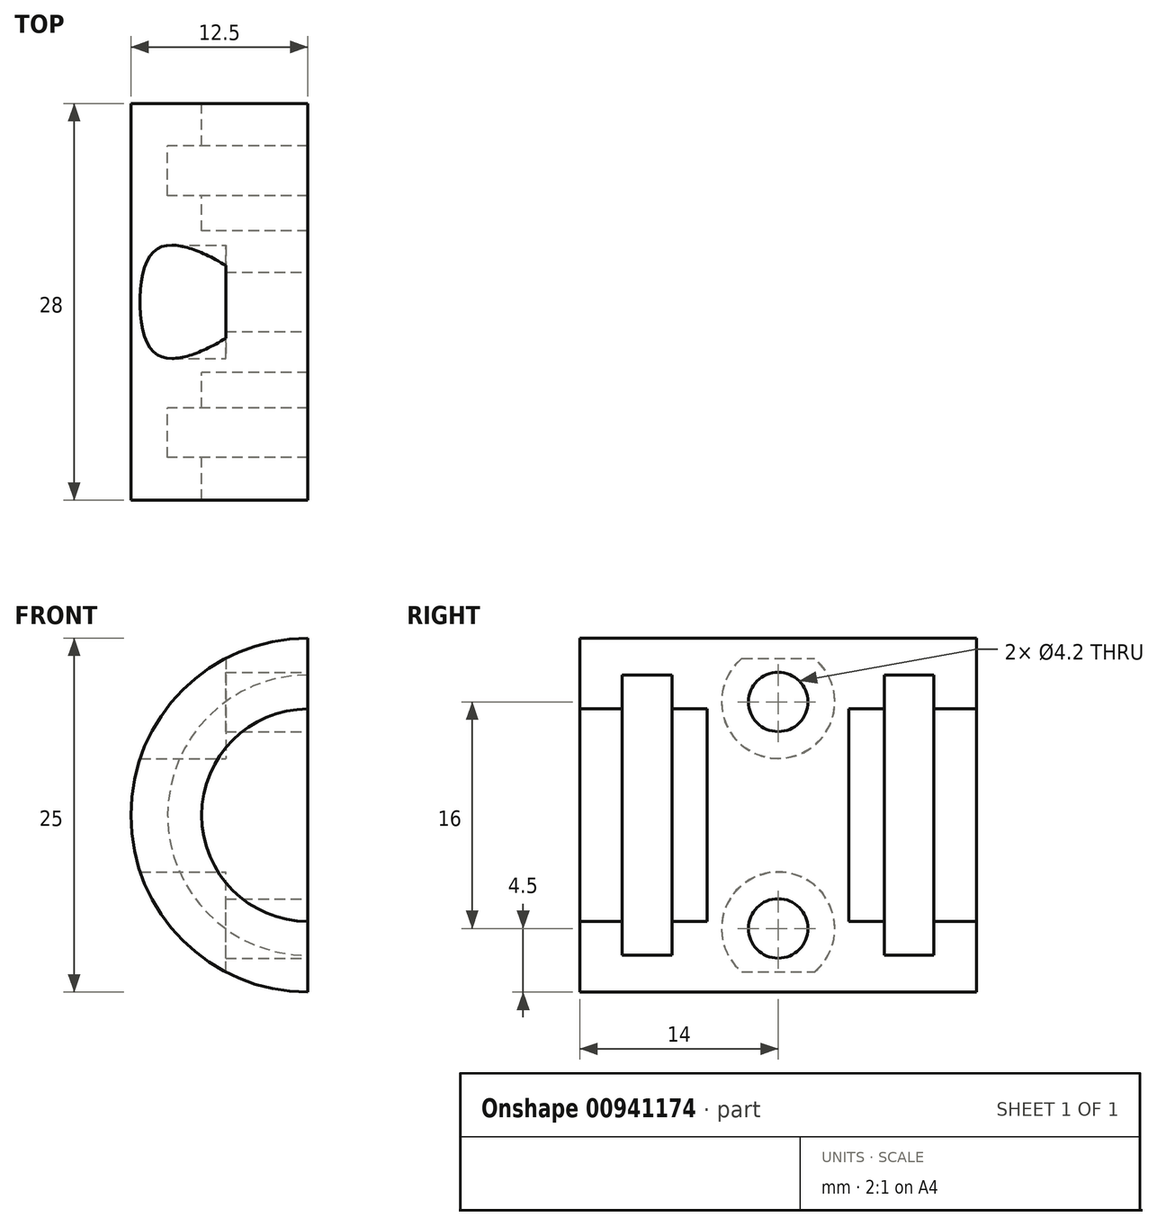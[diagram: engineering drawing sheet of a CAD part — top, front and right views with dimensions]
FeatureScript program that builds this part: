
annotation { "Feature Type Name" : "Feature", "Feature Type Description" : "" }
export const myFeature = defineFeature(function(context is Context, id is Id, definition is map)
    precondition{}
    {
        {
            var Q0;
            Q0=qCreatedBy(makeId("Front.planeOp"),FACE);
            var sketch = newSketch(context, id + "F0", { "sketchPlane" : qUnion([Q0])});
            skCircle(sketch, "E0", {"center": v(0, 0) * mm, "radius": 12.5 * mm});
            skCircle(sketch, "E1", {"center": v(0, 0) * mm, "radius": 7.5 * mm});
            skSolve(sketch);
        }
        {
            var Q0;
            Q0=makeQuery(id+"F0.imprint","IMPRINT",FACE,{"disambiguationData":[TD([[makeQuery(id+"F0.imprint","IMPRINT",EDGE,{"derivedFrom":sQuery(id+"F0.wireOp",EDGE,"E0")}),1.0]])]});
            extrude(context, id + "F1", {"entities" : qUnion([Q0]), "depth" : 28 * mm, "offsetDistance" : 25 * mm});
        }
        {
            var Q0;
            Q0=qCreatedBy(makeId("Right.planeOp"),FACE);
            var sketch = newSketch(context, id + "F2", { "sketchPlane" : qUnion([Q0])});
            skLineSegment(sketch, "E2.bottom", {"start": v(-21.5, 9.9) * mm, "end": v(-25, 9.9) * mm});
            skLineSegment(sketch, "E2.top", {"start": v(-21.5, -9.9) * mm, "end": v(-25, -9.9) * mm});
            skLineSegment(sketch, "E2.left", {"start": v(-21.5, 9.9) * mm, "end": v(-21.5, -9.9) * mm});
            skLineSegment(sketch, "E2.right", {"start": v(-25, 9.9) * mm, "end": v(-25, -9.9) * mm});
            skPoint(sketch, "E2.middle", {"position": v(-23.25, 0) * mm});
            skLineSegment(sketch, "E3.bottom", {"start": v(-3, 9.9) * mm, "end": v(-6.5, 9.9) * mm});
            skLineSegment(sketch, "E3.top", {"start": v(-3, -9.9) * mm, "end": v(-6.5, -9.9) * mm});
            skLineSegment(sketch, "E3.left", {"start": v(-3, 9.9) * mm, "end": v(-3, -9.9) * mm});
            skLineSegment(sketch, "E3.right", {"start": v(-6.5, 9.9) * mm, "end": v(-6.5, -9.9) * mm});
            skPoint(sketch, "E3.middle", {"position": v(-4.75, 0) * mm});
            skLineSegment(sketch, "E4", {"start": v(-23.25, 0) * mm, "end": v(21.1, 0) * mm});
            skLineSegment(sketch, "E5", {"start": v(21.1, 0) * mm, "end": v(-23.25, 0) * mm});
            skLineSegment(sketch, "E6", {"start": v(-34.97, 0) * mm, "end": v(-23.25, 0) * mm});
            skLineSegment(sketch, "E7", {"start": v(-32.13, 2.52) * mm, "end": v(11.78, 2.52) * mm});
            skSolve(sketch);
        }
        {
            var Q0;
            {var subQ0=sQuery(id+"F2.wireOp",EDGE,"E2.bottom");Q0=makeQuery(id+"F2.imprint","IMPRINT",FACE,{"disambiguationData":[TD([[makeQuery(id+"F2.imprint","IMPRINT",EDGE,{"derivedFrom":subQ0}),1.0]])]});}
            var Q1;
            {var subQ0=sQuery(id+"F2.wireOp",EDGE,"E3.bottom");Q1=makeQuery(id+"F2.imprint","IMPRINT",FACE,{"disambiguationData":[TD([[makeQuery(id+"F2.imprint","IMPRINT",EDGE,{"derivedFrom":subQ0}),1.0]])]});}
            var Q2;
            Q2=sQuery(id+"F2.wireOp",EDGE,"E6");
            revolve(context, id + "F3", {"operationType" : NewBodyOperationType.REMOVE, "surfaceOperationType" : NewSurfaceOperationType.NEW, "entities" : qUnion([Q0, Q1]), "axis" : qUnion([Q2]), "revolveType" : RevolveType.FULL, "oppositeDirection" : true});
        }
        {
            var Q0;
            Q0=makeQuery(id+"F1.opExtrude","CAP_FACE",FACE,{"disambiguationData":[OSD([sQuery(id+"F0.wireOp",EDGE,"E0"),sQuery(id+"F0.wireOp",EDGE,"E1")])],"isStart":false});
            var Q1;
            Q1=makeQuery(id+"F1.opExtrude","CAP_FACE",FACE,{"disambiguationData":[OSD([sQuery(id+"F0.wireOp",EDGE,"E0"),sQuery(id+"F0.wireOp",EDGE,"E1")])],"isStart":true});
            cPlane(context, id + "F4", {"entities" : qUnion([Q0, Q1]), "cplaneType" : CPlaneType.MID_PLANE, "offset" : 25 * mm, "width" : 150 * mm, "height" : 150 * mm});
        }
        {
            var Q0;
            Q0=qCreatedBy(id+"F4.planeOp",FACE);
            var sketch = newSketch(context, id + "F5", { "sketchPlane" : qUnion([Q0])});
            skCircle(sketch, "E8", {"center": v(0, 0) * mm, "radius": 8.5 * mm});
            skCircle(sketch, "E9", {"center": v(0, 0) * mm, "radius": 16.22 * mm});
            skSolve(sketch);
        }
        {
            var Q0;
            Q0=makeQuery(id+"F5.imprint","IMPRINT",FACE,{"disambiguationData":[TD([[makeQuery(id+"F5.imprint","IMPRINT",EDGE,{"derivedFrom":sQuery(id+"F5.wireOp",EDGE,"E8")}),1.0]])]});
            extrude(context, id + "F6", {"entities" : qUnion([Q0]), "operationType" : NewBodyOperationType.ADD, "endBound" : BoundingType.SYMMETRIC, "depth" : 10 * mm, "offsetDistance" : 25 * mm});
        }
        {
            var Q0;
            Q0=qCreatedBy(makeId("Right.planeOp"),FACE);
            var sketch = newSketch(context, id + "F7", { "sketchPlane" : qUnion([Q0])});
            skLineSegment(sketch, "E10", {"start": v(0, 0) * mm, "end": v(-28, 0) * mm});
            skLineSegment(sketch, "E11", {"start": v(-14, 0) * mm, "end": v(-14, 8) * mm});
            skLineSegment(sketch, "E12", {"start": v(-14, 8) * mm, "end": v(-14, 0) * mm});
            skLineSegment(sketch, "E13", {"start": v(-14, -8) * mm, "end": v(-14, 0) * mm});
            skCircle(sketch, "E14", {"center": v(-14, 8) * mm, "radius": 2.1 * mm});
            skCircle(sketch, "E15", {"center": v(-14, -8) * mm, "radius": 2.1 * mm});
            skSolve(sketch);
        }
        {
            var Q0;
            Q0=makeQuery(id+"F1.opExtrude","CAP_FACE",FACE,{"disambiguationData":[OSD([sQuery(id+"F0.wireOp",EDGE,"E0"),sQuery(id+"F0.wireOp",EDGE,"E1")])],"isStart":false});
            var sketch = newSketch(context, id + "F8", { "sketchPlane" : qUnion([Q0])});
            skLineSegment(sketch, "E16", {"start": v(0, -2.16) * mm, "end": v(0, 25.02) * mm});
            skLineSegment(sketch, "E17", {"start": v(0, 25.02) * mm, "end": v(20.81, 25.02) * mm});
            skLineSegment(sketch, "E18", {"start": v(20.81, 25.02) * mm, "end": v(20.81, -22.7) * mm});
            skLineSegment(sketch, "E19", {"start": v(20.81, -22.7) * mm, "end": v(0, -22.7) * mm});
            skLineSegment(sketch, "E20", {"start": v(0, -22.7) * mm, "end": v(0, -2.16) * mm});
            skSolve(sketch);
        }
        {
            var Q0;
            {var subQ0=sQuery(id+"F8.wireOp",EDGE,"E16");var subQ1=makeQuery(id+"F1.opExtrude","CAP_EDGE",EDGE,{"disambiguationData":[OSD([sQuery(id+"F0.wireOp",EDGE,"E0")])],"isStart":false});var subQ2=makeQuery(id+"F8.imprint","INTERSECT",VERTEX,{"derivedFrom":[subQ1,subQ0]});Q0=makeQuery(id+"F8.imprint","IMPRINT",FACE,{"disambiguationData":[TD([[makeQuery(id+"F8.imprint","IMPRINT",EDGE,{"disambiguationData":[TD([[subQ2,1.0]])],"derivedFrom":subQ0}),-1.0]])]});}
            var Q1;
            {var subQ0=sQuery(id+"F8.wireOp",EDGE,"E20");var subQ1=sQuery(id+"F8.wireOp",EDGE,"E16");var subQ2=makeQuery(id+"F8.imprint","INTERSECT",VERTEX,{"derivedFrom":[subQ1,subQ0]});Q1=makeQuery(id+"F8.imprint","IMPRINT",FACE,{"disambiguationData":[TD([[makeQuery(id+"F8.imprint","IMPRINT",EDGE,{"disambiguationData":[TD([[subQ2,-1.0]])],"derivedFrom":subQ1}),-1.0]])]});}
            extrude(context, id + "F9", {"entities" : qUnion([Q0, Q1]), "operationType" : NewBodyOperationType.REMOVE, "oppositeDirection" : true, "depth" : 30 * mm, "offsetDistance" : 25 * mm});
        }
        {
            var Q0;
            Q0=makeQuery(id+"F7.imprint","IMPRINT",FACE,{"disambiguationData":[TD([[makeQuery(id+"F7.imprint","IMPRINT",EDGE,{"derivedFrom":sQuery(id+"F7.wireOp",EDGE,"E15")}),1.0]])]});
            var Q1;
            Q1=makeQuery(id+"F7.imprint","IMPRINT",FACE,{"disambiguationData":[TD([[makeQuery(id+"F7.imprint","IMPRINT",EDGE,{"derivedFrom":sQuery(id+"F7.wireOp",EDGE,"E14")}),1.0]])]});
            extrude(context, id + "F10", {"entities" : qUnion([Q0, Q1]), "operationType" : NewBodyOperationType.REMOVE, "oppositeDirection" : true, "depth" : 25 * mm, "offsetDistance" : 25 * mm});
        }
        {
            var Q0;
            Q0=qCreatedBy(makeId("Right.planeOp"),FACE);
            var sketch = newSketch(context, id + "F11", { "sketchPlane" : qUnion([Q0])});
            skPoint(sketch, "E21.0", {"position": v(-14, 8) * mm});
            skPoint(sketch, "E22.0", {"position": v(-14, -8) * mm});
            skCircle(sketch, "E23", {"center": v(-14, -8) * mm, "radius": 4 * mm});
            skCircle(sketch, "E24", {"center": v(-14, 8) * mm, "radius": 4 * mm});
            skSolve(sketch);
        }
        {
            var Q0;
            Q0=makeQuery(id+"F11.imprint","IMPRINT",FACE,{"disambiguationData":[TD([[makeQuery(id+"F11.imprint","IMPRINT",EDGE,{"derivedFrom":sQuery(id+"F11.wireOp",EDGE,"E23")}),1.0]])]});
            var Q1;
            Q1=makeQuery(id+"F11.imprint","IMPRINT",FACE,{"disambiguationData":[TD([[makeQuery(id+"F11.imprint","IMPRINT",EDGE,{"derivedFrom":sQuery(id+"F11.wireOp",EDGE,"E24")}),1.0]])]});
            extrude(context, id + "F12", {"entities" : qUnion([Q0, Q1]), "operationType" : NewBodyOperationType.REMOVE, "oppositeDirection" : true, "depth" : 25 * mm, "offsetDistance" : 25 * mm, "hasSecondDirection" : true, "secondDirectionOppositeDirection" : true, "secondDirectionDepth" : 5.8 * mm});
        }
    });
